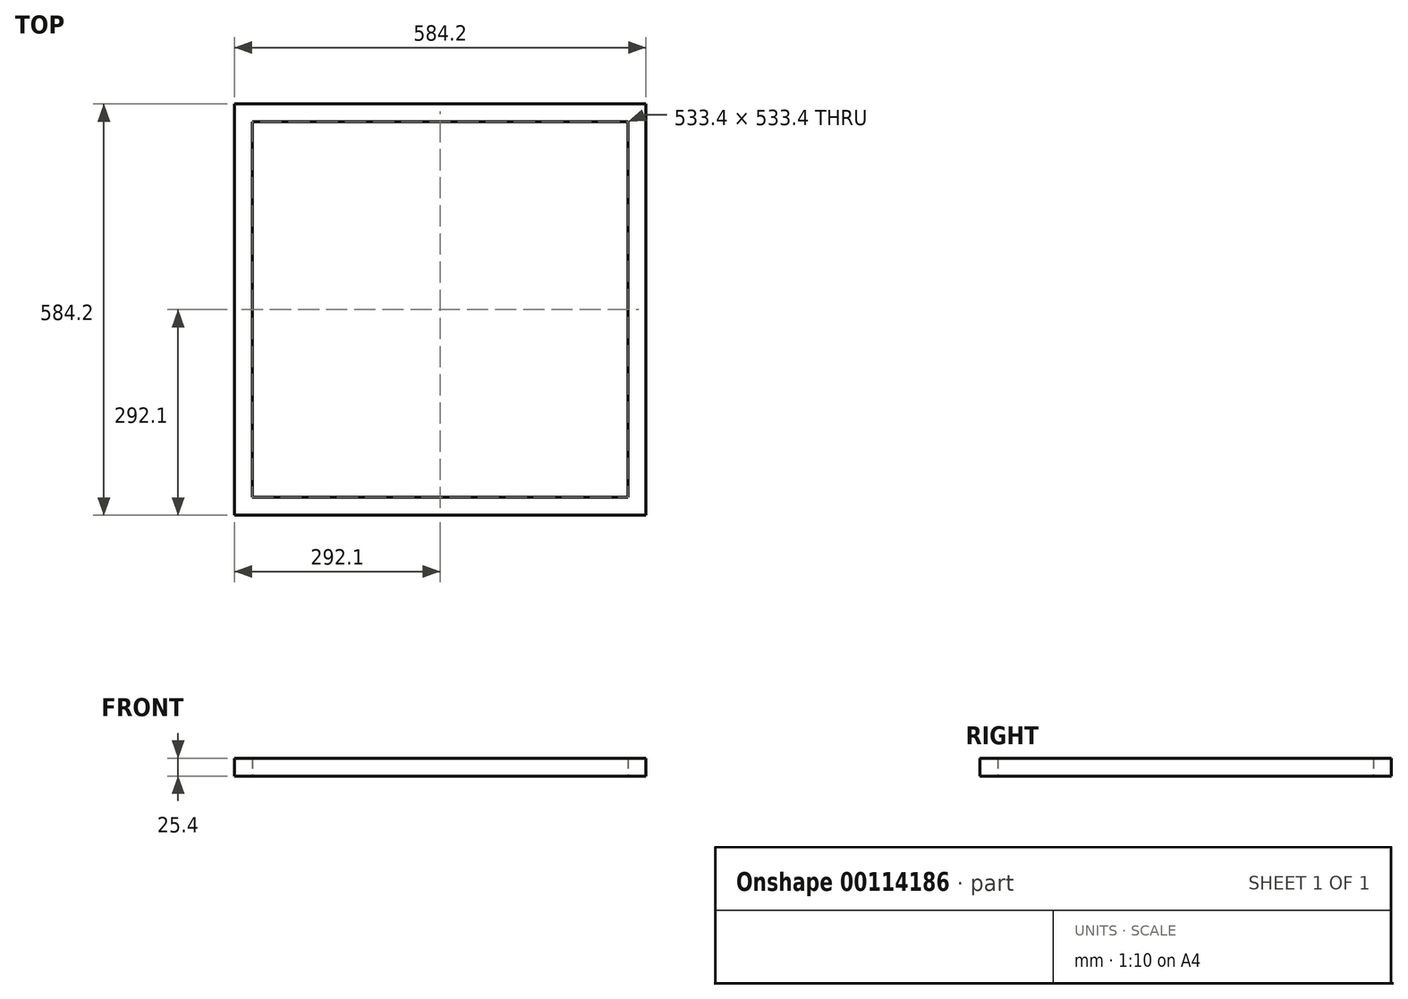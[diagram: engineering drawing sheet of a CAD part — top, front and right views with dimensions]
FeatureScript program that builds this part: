
annotation { "Feature Type Name" : "Feature", "Feature Type Description" : "" }
export const myFeature = defineFeature(function(context is Context, id is Id, definition is map)
    precondition{}
    {
        {
            var Q0;
            Q0=qCreatedBy(makeId("Top.planeOp"),FACE);
            var sketch = newSketch(context, id + "F0", { "sketchPlane" : qUnion([Q0])});
            skLineSegment(sketch, "E0.bottom", {"start": v(-292.1, 292.1) * mm, "end": v(292.1, 292.1) * mm});
            skLineSegment(sketch, "E0.top", {"start": v(-292.1, -292.1) * mm, "end": v(292.1, -292.1) * mm});
            skLineSegment(sketch, "E0.left", {"start": v(-292.1, 292.1) * mm, "end": v(-292.1, -292.1) * mm});
            skLineSegment(sketch, "E0.right", {"start": v(292.1, 292.1) * mm, "end": v(292.1, -292.1) * mm});
            skPoint(sketch, "E0.middle", {"position": v(0, 0) * mm});
            skLineSegment(sketch, "E1.bottom", {"start": v(292.1, 292.1) * mm, "end": v(-292.1, 292.1) * mm});
            skLineSegment(sketch, "E1.top", {"start": v(292.1, -292.1) * mm, "end": v(-292.1, -292.1) * mm});
            skLineSegment(sketch, "E2.bottom", {"start": v(-266.7, 266.7) * mm, "end": v(266.7, 266.7) * mm});
            skLineSegment(sketch, "E2.top", {"start": v(-266.7, -266.7) * mm, "end": v(266.7, -266.7) * mm});
            skLineSegment(sketch, "E2.left", {"start": v(-266.7, 266.7) * mm, "end": v(-266.7, -266.7) * mm});
            skLineSegment(sketch, "E2.right", {"start": v(266.7, 266.7) * mm, "end": v(266.7, -266.7) * mm});
            skSolve(sketch);
        }
        {
            var Q0;
            Q0 = qSketchRegion(id + "F0", true);
            var Q1;
            Q1=makeQuery(id+"F0.imprint","IMPRINT",FACE,{"disambiguationData":[TD([[makeQuery(id+"F0.imprint","IMPRINT",EDGE,{"derivedFrom":sQuery(id+"F0.wireOp",EDGE,"E1.bottom")}),1.0]])]});
            extrude(context, id + "F1", {"entities" : qUnion([Q0, Q1]), "depth" : 25.4 * mm});
        }
    });
